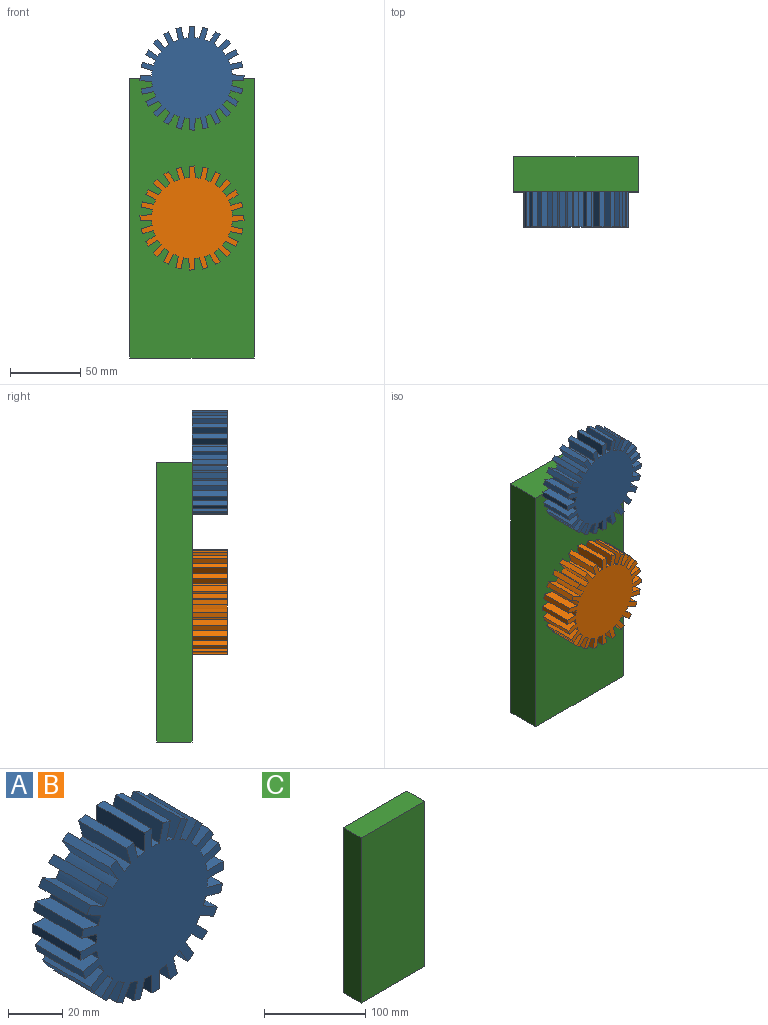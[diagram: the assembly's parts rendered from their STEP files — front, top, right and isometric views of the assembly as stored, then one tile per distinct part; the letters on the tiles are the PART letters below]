
ASSEMBLY  parts=3 mates=2
PART A: 98 faces, bbox 74.1x25x74.1 mm
  f0: plane 25x8.32mm, normal (1,0,0), area 207.9mm2, adj f1,f95,f96,f97
  f1: cylinder r=28.95mm len=25mm, axis (0,1,0), area 95mm2, adj f0,f2,f96,f97
  f2: plane 25x7.8mm, normal (-0.97,0,-0.26), area 201.8mm2, adj f1,f3,f96,f97
  f3: plane 25x3.64mm, normal (0.26,0,-0.97), area 94.2mm2, adj f2,f4,f96,f97
  f4: plane 25x8.03mm, normal (0.97,0,0.26), area 207.9mm2, adj f3,f5,f96,f97
  f5: cylinder r=28.95mm len=25mm, axis (0,1,0), area 95mm2, adj f4,f6,f96,f97
  f6: plane 25x6.99mm, normal (-0.87,0,-0.5), area 201.8mm2, adj f5,f7,f96,f97
  f7: plane 25x3.26mm, normal (0.5,0,-0.87), area 94.2mm2, adj f6,f8,f96,f97
  f8: plane 25x7.2mm, normal (0.87,0,0.5), area 207.9mm2, adj f7,f9,f96,f97
  f9: cylinder r=28.95mm len=25mm, axis (0,1,0), area 95mm2, adj f8,f10,f96,f97
  f10: plane 25x5.71mm, normal (-0.71,0,-0.71), area 201.8mm2, adj f9,f11,f96,f97
  f11: plane 25x2.66mm, normal (0.71,0,-0.71), area 94.2mm2, adj f10,f12,f96,f97
  f12: plane 25x5.88mm, normal (0.71,0,0.71), area 207.9mm2, adj f11,f13,f96,f97
  f13: cylinder r=28.95mm len=25mm, axis (0,1,0), area 95mm2, adj f12,f14,f96,f97
  f14: plane 25x6.99mm, normal (-0.5,0,-0.87), area 201.8mm2, adj f13,f15,f96,f97
  f15: plane 25x3.26mm, normal (0.87,0,-0.5), area 94.2mm2, adj f14,f16,f96,f97
  f16: plane 25x7.2mm, normal (0.5,0,0.87), area 207.9mm2, adj f15,f17,f96,f97
  f17: cylinder r=28.95mm len=25mm, axis (0,1,0), area 95mm2, adj f16,f18,f96,f97
  f18: plane 25x7.8mm, normal (-0.26,0,-0.97), area 201.8mm2, adj f17,f19,f96,f97
  f19: plane 25x3.64mm, normal (0.97,0,-0.26), area 94.2mm2, adj f18,f20,f96,f97
  f20: plane 25x8.03mm, normal (0.26,0,0.97), area 207.9mm2, adj f19,f21,f96,f97
  f21: cylinder r=28.95mm len=25mm, axis (0,1,0), area 95mm2, adj f20,f22,f96,f97
  f22: plane 25x8.07mm, normal (0,0,-1), area 201.8mm2, adj f21,f23,f96,f97
  f23: plane 25x3.77mm, normal (1,0,0), area 94.2mm2, adj f22,f24,f96,f97
  f24: plane 25x8.32mm, normal (0,0,1), area 207.9mm2, adj f23,f25,f96,f97
  f25: cylinder r=28.95mm len=25mm, axis (0,1,0), area 95mm2, adj f24,f26,f96,f97
  f26: plane 25x7.8mm, normal (0.26,0,-0.97), area 201.8mm2, adj f25,f27,f96,f97
  f27: plane 25x3.64mm, normal (0.97,0,0.26), area 94.2mm2, adj f26,f28,f96,f97
  f28: plane 25x8.03mm, normal (-0.26,0,0.97), area 207.9mm2, adj f27,f29,f96,f97
  f29: cylinder r=28.95mm len=25mm, axis (0,1,0), area 95mm2, adj f28,f30,f96,f97
  f30: plane 25x6.99mm, normal (0.5,0,-0.87), area 201.8mm2, adj f29,f31,f96,f97
  f31: plane 25x3.26mm, normal (0.87,0,0.5), area 94.2mm2, adj f30,f32,f96,f97
  f32: plane 25x7.2mm, normal (-0.5,0,0.87), area 207.9mm2, adj f31,f33,f96,f97
  f33: cylinder r=28.95mm len=25mm, axis (0,1,0), area 95mm2, adj f32,f34,f96,f97
  f34: plane 25x5.71mm, normal (0.71,0,-0.71), area 201.8mm2, adj f33,f35,f96,f97
  f35: plane 25x2.66mm, normal (0.71,0,0.71), area 94.2mm2, adj f34,f36,f96,f97
  f36: plane 25x5.88mm, normal (-0.71,0,0.71), area 207.9mm2, adj f35,f37,f96,f97
  f37: cylinder r=28.95mm len=25mm, axis (0,1,0), area 95mm2, adj f36,f38,f96,f97
  f38: plane 25x6.99mm, normal (0.87,0,-0.5), area 201.8mm2, adj f37,f39,f96,f97
  f39: plane 25x3.26mm, normal (0.5,0,0.87), area 94.2mm2, adj f38,f40,f96,f97
  f40: plane 25x7.2mm, normal (-0.87,0,0.5), area 207.9mm2, adj f39,f41,f96,f97
  f41: cylinder r=28.95mm len=25mm, axis (0,1,0), area 95mm2, adj f40,f42,f96,f97
  f42: plane 25x7.8mm, normal (0.97,0,-0.26), area 201.8mm2, adj f41,f43,f96,f97
  f43: plane 25x3.64mm, normal (0.26,0,0.97), area 94.2mm2, adj f42,f44,f96,f97
  f44: plane 25x8.03mm, normal (-0.97,0,0.26), area 207.9mm2, adj f43,f45,f96,f97
  f45: cylinder r=28.95mm len=25mm, axis (0,1,0), area 95mm2, adj f44,f46,f96,f97
  f46: plane 25x8.07mm, normal (1,0,0), area 201.8mm2, adj f45,f47,f96,f97
  f47: plane 25x3.77mm, normal (0,0,1), area 94.2mm2, adj f46,f48,f96,f97
  f48: plane 25x8.32mm, normal (-1,0,0), area 207.9mm2, adj f47,f49,f96,f97
  f49: cylinder r=28.95mm len=25mm, axis (0,1,0), area 95mm2, adj f48,f50,f96,f97
  f50: plane 25x7.8mm, normal (0.97,0,0.26), area 201.8mm2, adj f49,f51,f96,f97
  f51: plane 25x3.64mm, normal (-0.26,0,0.97), area 94.2mm2, adj f50,f52,f96,f97
  f52: plane 25x8.03mm, normal (-0.97,0,-0.26), area 207.9mm2, adj f51,f53,f96,f97
  f53: cylinder r=28.95mm len=25mm, axis (0,1,0), area 95mm2, adj f52,f54,f96,f97
  f54: plane 25x6.99mm, normal (0.87,0,0.5), area 201.8mm2, adj f53,f55,f96,f97
  f55: plane 25x3.26mm, normal (-0.5,0,0.87), area 94.2mm2, adj f54,f56,f96,f97
  f56: plane 25x7.2mm, normal (-0.87,0,-0.5), area 207.9mm2, adj f55,f57,f96,f97
  f57: cylinder r=28.95mm len=25mm, axis (0,1,0), area 95mm2, adj f56,f58,f96,f97
  f58: plane 25x5.71mm, normal (0.71,0,0.71), area 201.8mm2, adj f57,f59,f96,f97
  f59: plane 25x2.66mm, normal (-0.71,0,0.71), area 94.2mm2, adj f58,f60,f96,f97
  f60: plane 25x5.88mm, normal (-0.71,0,-0.71), area 207.9mm2, adj f59,f61,f96,f97
  f61: cylinder r=28.95mm len=25mm, axis (0,1,0), area 95mm2, adj f60,f62,f96,f97
  f62: plane 25x6.99mm, normal (0.5,0,0.87), area 201.8mm2, adj f61,f63,f96,f97
  f63: plane 25x3.26mm, normal (-0.87,0,0.5), area 94.2mm2, adj f62,f64,f96,f97
  f64: plane 25x7.2mm, normal (-0.5,0,-0.87), area 207.9mm2, adj f63,f65,f96,f97
  f65: cylinder r=28.95mm len=25mm, axis (0,1,0), area 95mm2, adj f64,f66,f96,f97
  f66: plane 25x7.8mm, normal (0.26,0,0.97), area 201.8mm2, adj f65,f67,f96,f97
  f67: plane 25x3.64mm, normal (-0.97,0,0.26), area 94.2mm2, adj f66,f68,f96,f97
  f68: plane 25x8.03mm, normal (-0.26,0,-0.97), area 207.9mm2, adj f67,f69,f96,f97
  f69: cylinder r=28.95mm len=25mm, axis (0,1,0), area 95mm2, adj f68,f70,f96,f97
  f70: plane 25x8.07mm, normal (0,0,1), area 201.8mm2, adj f69,f71,f96,f97
  f71: plane 25x3.77mm, normal (-1,0,0), area 94.2mm2, adj f70,f72,f96,f97
  f72: plane 25x8.32mm, normal (0,0,-1), area 207.9mm2, adj f71,f73,f96,f97
  f73: cylinder r=28.95mm len=25mm, axis (0,1,0), area 95mm2, adj f72,f74,f96,f97
  f74: plane 25x7.8mm, normal (-0.26,0,0.97), area 201.8mm2, adj f73,f75,f96,f97
  f75: plane 25x3.64mm, normal (-0.97,0,-0.26), area 94.2mm2, adj f74,f76,f96,f97
  f76: plane 25x8.03mm, normal (0.26,0,-0.97), area 207.9mm2, adj f75,f77,f96,f97
  f77: cylinder r=28.95mm len=25mm, axis (0,1,0), area 95mm2, adj f76,f78,f96,f97
  f78: plane 25x6.99mm, normal (-0.5,0,0.87), area 201.8mm2, adj f77,f79,f96,f97
  f79: plane 25x3.26mm, normal (-0.87,0,-0.5), area 94.2mm2, adj f78,f80,f96,f97
  f80: plane 25x7.2mm, normal (0.5,0,-0.87), area 207.9mm2, adj f79,f81,f96,f97
  f81: cylinder r=28.95mm len=25mm, axis (0,1,0), area 95mm2, adj f80,f82,f96,f97
  f82: plane 25x5.71mm, normal (-0.71,0,0.71), area 201.8mm2, adj f81,f83,f96,f97
  f83: plane 25x2.66mm, normal (-0.71,0,-0.71), area 94.2mm2, adj f82,f84,f96,f97
  f84: plane 25x5.88mm, normal (0.71,0,-0.71), area 207.9mm2, adj f83,f85,f96,f97
  f85: cylinder r=28.95mm len=25mm, axis (0,1,0), area 95mm2, adj f84,f86,f96,f97
  f86: plane 25x6.99mm, normal (-0.87,0,0.5), area 201.8mm2, adj f85,f87,f96,f97
  f87: plane 25x3.26mm, normal (-0.5,0,-0.87), area 94.2mm2, adj f86,f88,f96,f97
  f88: plane 25x7.2mm, normal (0.87,0,-0.5), area 207.9mm2, adj f87,f89,f96,f97
  f89: cylinder r=28.95mm len=25mm, axis (0,1,0), area 95mm2, adj f88,f90,f96,f97
  f90: plane 25x7.8mm, normal (-0.97,0,0.26), area 201.8mm2, adj f89,f91,f96,f97
  f91: plane 25x3.64mm, normal (-0.26,0,-0.97), area 94.2mm2, adj f90,f92,f96,f97
  f92: plane 25x8.03mm, normal (0.97,0,-0.26), area 207.9mm2, adj f91,f93,f96,f97
  f93: cylinder r=28.95mm len=25mm, axis (0,1,0), area 95mm2, adj f92,f94,f96,f97
  f94: plane 25x8.07mm, normal (-1,0,0), area 201.8mm2, adj f93,f95,f96,f97
  f95: plane 25x3.77mm, normal (0,0,-1), area 94.2mm2, adj f0,f94,f96,f97
  f96: plane 74.05x74.05mm, normal (0,-1,0), area 3371.2mm2, adj f0,f1,f2,f3,f4,f5,f6,f7
  f97: plane 74.05x74.05mm, normal (0,1,0), area 3371.2mm2, adj f0,f1,f2,f3,f4,f5,f6,f7
PART B: same geometry as A
PART C: 6 faces, bbox 88.8x25x199.9 mm
  f0: plane 199.88x25mm, normal (1,0,0), area 4997mm2, adj f1,f3,f4,f5
  f1: plane 88.83x25mm, normal (0,0,1), area 2220.8mm2, adj f0,f2,f4,f5
  f2: plane 199.88x25mm, normal (-1,0,0), area 4997mm2, adj f1,f3,f4,f5
  f3: plane 88.83x25mm, normal (0,0,-1), area 2220.8mm2, adj f0,f2,f4,f5
  f4: plane 199.88x88.83mm, normal (0,-1,0), area 17755.7mm2, adj f0,f1,f2,f3
  f5: plane 199.88x88.83mm, normal (0,1,0), area 17755.7mm2, adj f0,f1,f2,f3
PLACE A rot(axis=(0,-1,0),42.1deg) t=(-121.58,-23.67,130.02)mm
PLACE B rot(axis=(-0.93,0,0.36),180deg) t=(-121.58,-48.67,30.08)mm
PLACE C rot(axis=(1,0,0),180deg) t=(-9.5,-23.67,-7.18)mm
MATE revolute A.f1 <-> C.f5  axis (0,1,0) through (-121.58,-23.67,130.02)mm
MATE revolute B.f93 <-> C.f5  axis (0,1,0) through (-121.58,-23.67,30.08)mm
